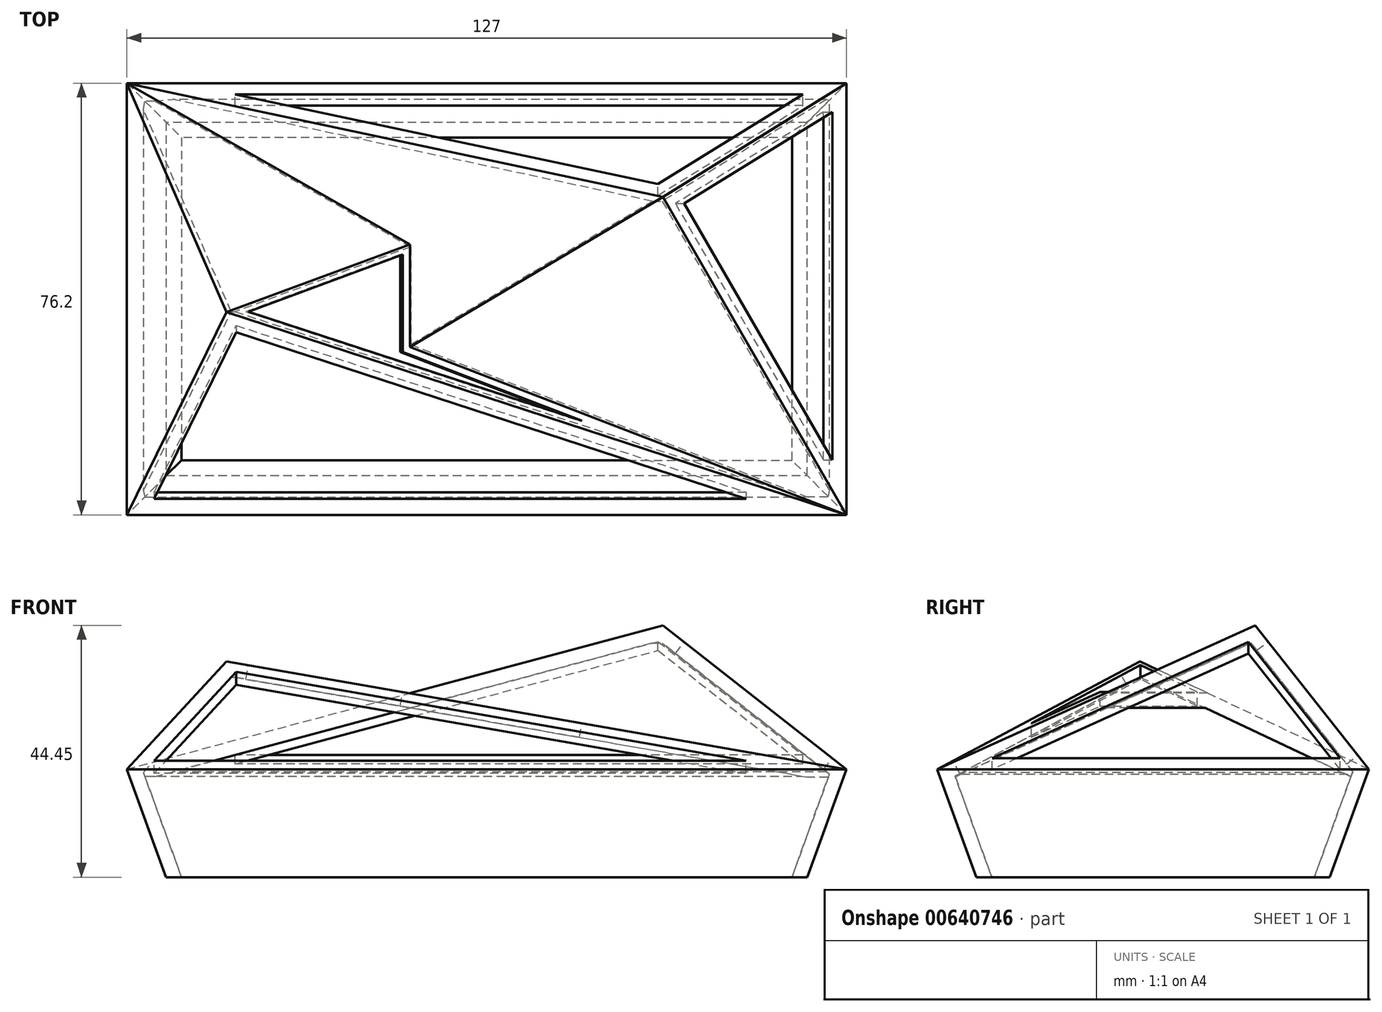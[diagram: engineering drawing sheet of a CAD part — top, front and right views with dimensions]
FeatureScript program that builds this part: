
annotation { "Feature Type Name" : "Feature", "Feature Type Description" : "" }
export const myFeature = defineFeature(function(context is Context, id is Id, definition is map)
    precondition{}
    {
        {
            var Q0;
            Q0=qCreatedBy(makeId("Top.planeOp"),FACE);
            var sketch = newSketch(context, id + "F0", { "sketchPlane" : qUnion([Q0])});
            skLineSegment(sketch, "E0.bottom", {"start": v(63.5, -38.1) * mm, "end": v(-63.5, -38.1) * mm});
            skLineSegment(sketch, "E0.top", {"start": v(63.5, 38.1) * mm, "end": v(-63.5, 38.1) * mm});
            skLineSegment(sketch, "E0.left", {"start": v(63.5, -38.1) * mm, "end": v(63.5, 38.1) * mm});
            skLineSegment(sketch, "E0.right", {"start": v(-63.5, -38.1) * mm, "end": v(-63.5, 38.1) * mm});
            skPoint(sketch, "E0.middle", {"position": v(0, 0) * mm});
            skSolve(sketch);
        }
        {
            var Q0;
            Q0=qCreatedBy(makeId("Top.planeOp"),FACE);
            cPlane(context, id + "F1", {"entities" : qUnion([Q0]), "cplaneType" : CPlaneType.OFFSET, "offset" : 25.4 * mm, "width" : 152.4 * mm, "height" : 152.4 * mm});
        }
        {
            var Q0;
            Q0=qCreatedBy(id+"F1.planeOp",FACE);
            var sketch = newSketch(context, id + "F2", { "sketchPlane" : qUnion([Q0])});
            skPoint(sketch, "E1", {"position": v(31.08, 18.02) * mm});
            skSolve(sketch);
        }
        {
            var Q0;
            Q0=makeQuery(id+"F0.imprint","IMPRINT",FACE,{"disambiguationData":[TD([[makeQuery(id+"F0.imprint","IMPRINT",EDGE,{"derivedFrom":sQuery(id+"F0.wireOp",EDGE,"E0.bottom")}),-1.0]])]});
            var Q1;
            Q1=sQuery(id+"F2.wireOp",VERTEX,"E1");
            loft(context, id + "F3", {"sheetProfilesArray" : [{ "sheetProfileEntities" : qUnion([Q0]) }, { "sheetProfileEntities" : qUnion([Q1]) }]});
        }
        {
            var Q0;
            Q0=qCreatedBy(makeId("Top.planeOp"),FACE);
            cPlane(context, id + "F4", {"entities" : qUnion([Q0]), "cplaneType" : CPlaneType.OFFSET, "offset" : 19.05 * mm, "width" : 152.4 * mm, "height" : 152.4 * mm});
        }
        {
            var Q0;
            Q0=qCreatedBy(id+"F4.planeOp",FACE);
            var sketch = newSketch(context, id + "F5", { "sketchPlane" : qUnion([Q0])});
            skPoint(sketch, "E2", {"position": v(-45.92, -2.32) * mm});
            skSolve(sketch);
        }
        {
            var Q1;
            Q1 = qSketchRegion(id + "F0", true);
            var Q2;
            Q2=sQuery(id+"F5.wireOp",VERTEX,"E2");
            loft(context, id + "F6", {"operationType" : NewBodyOperationType.ADD, "sheetProfilesArray" : [{ "sheetProfileEntities" : qUnion([Q1]) }, { "sheetProfileEntities" : qUnion([Q2]) }]});
        }
        {
            var Q0;
            Q0 = qSketchRegion(id + "F0", true);
            extrude(context, id + "F7", {"entities" : qUnion([Q0]), "operationType" : NewBodyOperationType.ADD, "oppositeDirection" : true, "depth" : 19.05 * mm, "offsetDistance" : 25.4 * mm, "hasDraft" : true, "draftAngle" : 20 * degree, "draftPullDirection" : true});
        }
        {
            var Q0;
            Q0=makeQuery(id+"F7.opExtrude","CAP_FACE",FACE,{"disambiguationData":[OSD([sQuery(id+"F0.wireOp",EDGE,"E0.bottom"),sQuery(id+"F0.wireOp",EDGE,"E0.top"),sQuery(id+"F0.wireOp",EDGE,"E0.left"),sQuery(id+"F0.wireOp",EDGE,"E0.right")])],"isStart":false});
            shell(context, id + "F8", {"entities" : qUnion([Q0]), "thickness" : 2.54 * mm});
        }
        {
            var Q0;
            Q0=makeQuery(id+"F3.opLoft","SWEPT_FACE",FACE,{"disambiguationData":[OSD([sQuery(id+"F0.wireOp",EDGE,"E0.bottom"),sQuery(id+"F0.wireOp",EDGE,"E0.top"),sQuery(id+"F0.wireOp",EDGE,"E0.left")])]});
            var sketch = newSketch(context, id + "F9", { "sketchPlane" : qUnion([Q0])});
            skLineSegment(sketch, "E3.0", {"start": v(46.81, 33.02) * mm, "end": v(13.6, 16.83) * mm});
            skLineSegment(sketch, "E3.1", {"start": v(46.81, -28.4) * mm, "end": v(46.81, 33.02) * mm});
            skLineSegment(sketch, "E3.2", {"start": v(13.6, 16.83) * mm, "end": v(46.81, -28.4) * mm});
            skSolve(sketch);
        }
        {
            var Q0;
            Q0 = qSketchRegion(id + "F9", true);
            extrude(context, id + "F10", {"entities" : qUnion([Q0]), "operationType" : NewBodyOperationType.REMOVE, "oppositeDirection" : true, "depth" : 7.62 * mm, "offsetDistance" : 25.4 * mm});
        }
        {
            var Q0;
            Q0=makeQuery(id+"F3.opLoft","SWEPT_FACE",FACE,{"disambiguationData":[OSD([sQuery(id+"F0.wireOp",EDGE,"E0.top"),sQuery(id+"F0.wireOp",EDGE,"E0.left"),sQuery(id+"F0.wireOp",EDGE,"E0.right")])]});
            var sketch = newSketch(context, id + "F11", { "sketchPlane" : qUnion([Q0])});
            skLineSegment(sketch, "E4.0", {"start": v(44.42, -20.45) * mm, "end": v(-30.23, 5.1) * mm});
            skLineSegment(sketch, "E4.1", {"start": v(-55.83, -20.45) * mm, "end": v(44.42, -20.45) * mm});
            skLineSegment(sketch, "E4.2", {"start": v(-30.23, 5.1) * mm, "end": v(-55.83, -20.45) * mm});
            skSolve(sketch);
        }
        {
            var Q0;
            Q0=makeQuery(id+"F11.imprint","IMPRINT",FACE,{"disambiguationData":[TD([[makeQuery(id+"F11.imprint","IMPRINT",EDGE,{"derivedFrom":sQuery(id+"F11.wireOp",EDGE,"E4.0")}),1.0]])]});
            extrude(context, id + "F12", {"entities" : qUnion([Q0]), "operationType" : NewBodyOperationType.REMOVE, "oppositeDirection" : true, "depth" : 12.7 * mm, "offsetDistance" : 25.4 * mm});
        }
        {
            var Q0;
            Q0=makeQuery(id+"F6.opLoft","SWEPT_FACE",FACE,{"disambiguationData":[OSD([sQuery(id+"F0.wireOp",EDGE,"E0.bottom"),sQuery(id+"F0.wireOp",EDGE,"E0.top"),sQuery(id+"F0.wireOp",EDGE,"E0.left")])]});
            var sketch = newSketch(context, id + "F13", { "sketchPlane" : qUnion([Q0])});
            skLineSegment(sketch, "E5.0", {"start": v(15.17, -21.5) * mm, "end": v(-16.92, -9.34) * mm});
            skLineSegment(sketch, "E5.1", {"start": v(-44.6, -2.25) * mm, "end": v(15.17, -21.5) * mm});
            skLineSegment(sketch, "E5.2", {"start": v(-16.92, 7.82) * mm, "end": v(-44.6, -2.25) * mm});
            skLineSegment(sketch, "E5.3", {"start": v(-16.92, -9.34) * mm, "end": v(-16.92, 7.82) * mm});
            skSolve(sketch);
        }
        {
            var Q0;
            Q0 = qSketchRegion(id + "F13", true);
            extrude(context, id + "F14", {"entities" : qUnion([Q0]), "operationType" : NewBodyOperationType.REMOVE, "oppositeDirection" : true, "depth" : 12.7 * mm, "offsetDistance" : 25.4 * mm});
        }
        {
            var Q0;
            Q0=makeQuery(id+"F6.opLoft","SWEPT_FACE",FACE,{"disambiguationData":[OSD([sQuery(id+"F0.wireOp",EDGE,"E0.bottom"),sQuery(id+"F0.wireOp",EDGE,"E0.left"),sQuery(id+"F0.wireOp",EDGE,"E0.right")])]});
            var sketch = newSketch(context, id + "F15", { "sketchPlane" : qUnion([Q0])});
            skLineSegment(sketch, "E6.0", {"start": v(45.79, -30.46) * mm, "end": v(-44.2, 2.88) * mm});
            skLineSegment(sketch, "E6.1", {"start": v(-58.66, -30.46) * mm, "end": v(45.79, -30.46) * mm});
            skLineSegment(sketch, "E6.2", {"start": v(-44.2, 2.88) * mm, "end": v(-58.66, -30.46) * mm});
            skSolve(sketch);
        }
        {
            var Q0;
            Q0=makeQuery(id+"F15.imprint","IMPRINT",FACE,{"disambiguationData":[TD([[makeQuery(id+"F15.imprint","IMPRINT",EDGE,{"derivedFrom":sQuery(id+"F15.wireOp",EDGE,"E6.0")}),1.0]])]});
            extrude(context, id + "F16", {"entities" : qUnion([Q0]), "operationType" : NewBodyOperationType.REMOVE, "oppositeDirection" : true, "depth" : 7.62 * mm, "offsetDistance" : 25.4 * mm});
        }
    });
